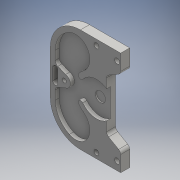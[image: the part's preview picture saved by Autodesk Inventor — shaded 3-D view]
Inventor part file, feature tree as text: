
AUTODESK INVENTOR PART (.ipt)
format: ipt  version: 2016 (Build 200138000, 138)  size: 294,912 bytes
history: native  units: mm
features: extrude x12, sketch x12, fillet x7
ambient origin geometry x8: Origin, YZ Plane, XZ Plane, XY Plane, X Axis, Y Axis, Z Axis, Center Point
bodies: Body1 (feature_tree)
feature tree (31):
  extrude  "Extrusion2"  Depth=103.0mm
  fillet  "Fillet3"  Radius=9.0mm
  fillet  "Fillet4"  Radius=30.0mm
  fillet  "Fillet5"  Radius=30.0mm
  extrude  "Extrusion3"  Depth=30.0mm
  extrude  "Extrusion4"  Depth=9.0mm
  extrude  "Extrusion5"  Depth=14.0mm
  fillet  "Fillet6"  Radius=9.0mm
  extrude  "Extrusion6"  Depth=18.0mm
  extrude  "Extrusion7"  Depth=4.0mm
  extrude  "Extrusion8"  Depth=3.5mm
  extrude  "Extrusion9"  Depth=5.0mm
  extrude  "Extrusion10"  Depth=5.0mm
  extrude  "Extrusion11"  Depth=5.0mm
  fillet  "Fillet7"  Radius=5.5mm
  fillet  "Fillet8"  Radius=9.0mm
  extrude  "Extrusion12"  Depth=4.0mm
  fillet  "Fillet9"  Radius=4.0mm
  extrude  "Extrusion13"  Depth=5.0mm
  sketch  "Sketch2"  dims[d6=103.0mm d7=103.0mm d8=9.0mm d9=0.0mm d10=30.0mm d11=30.0mm]
  sketch  "Sketch3"  dims[d12=30.0mm d13=33.0mm]
  sketch  "Sketch4"  dims[d14=9.0mm d15=0.0mm d16=26.0mm]
  sketch  "Sketch5"  dims[d17=26.0mm d18=14.0mm d19=9.0mm d20=0.0mm]
  sketch  "Sketch6"  dims[d21=18.0mm d22=18.0mm]
  sketch  "Sketch7"  dims[d23=9.0mm d24=0.0mm d25=4.0mm]
  sketch  "Sketch8"  dims[d26=8.5mm d27=3.5mm]
  sketch  "Sketch9"  dims[d28=5.0mm d29=8.5mm]
  sketch  "Sketch10"  dims[d30=5.0mm d31=24.0mm]
  sketch  "Sketch11"  dims[d32=5.5mm d33=5.0mm d34=5.5mm d35=9.0mm d36=0.0mm]
  sketch  "Sketch12"  dims[d37=10.0mm d38=34.0mm d39=4.0mm d40=0.0mm]
  sketch  "Sketch13"  dims[d41=5.0mm d42=0.0mm d43=5.0mm d44=5.0mm d45=32.0mm d46=32.0mm d47=2.5mm d48=4.0mm d49=0.0mm d52=5.0mm d53=5.0mm d54=4.0mm d55=0.0mm d56=5.0mm d57=5.0mm d58=4.0mm d59=0.0mm d60=14.0mm d61=14.0mm d62=15.0mm d63=10.0mm d64=15.0mm d65=10.0mm d66=12.0mm d67=4.0mm d68=0.0mm d69=4.0mm d70=4.0mm d71=5.0mm d72=6.0mm d73=6.0mm d74=5.0mm d75=5.0mm d76=9.0mm d77=0.0mm]
